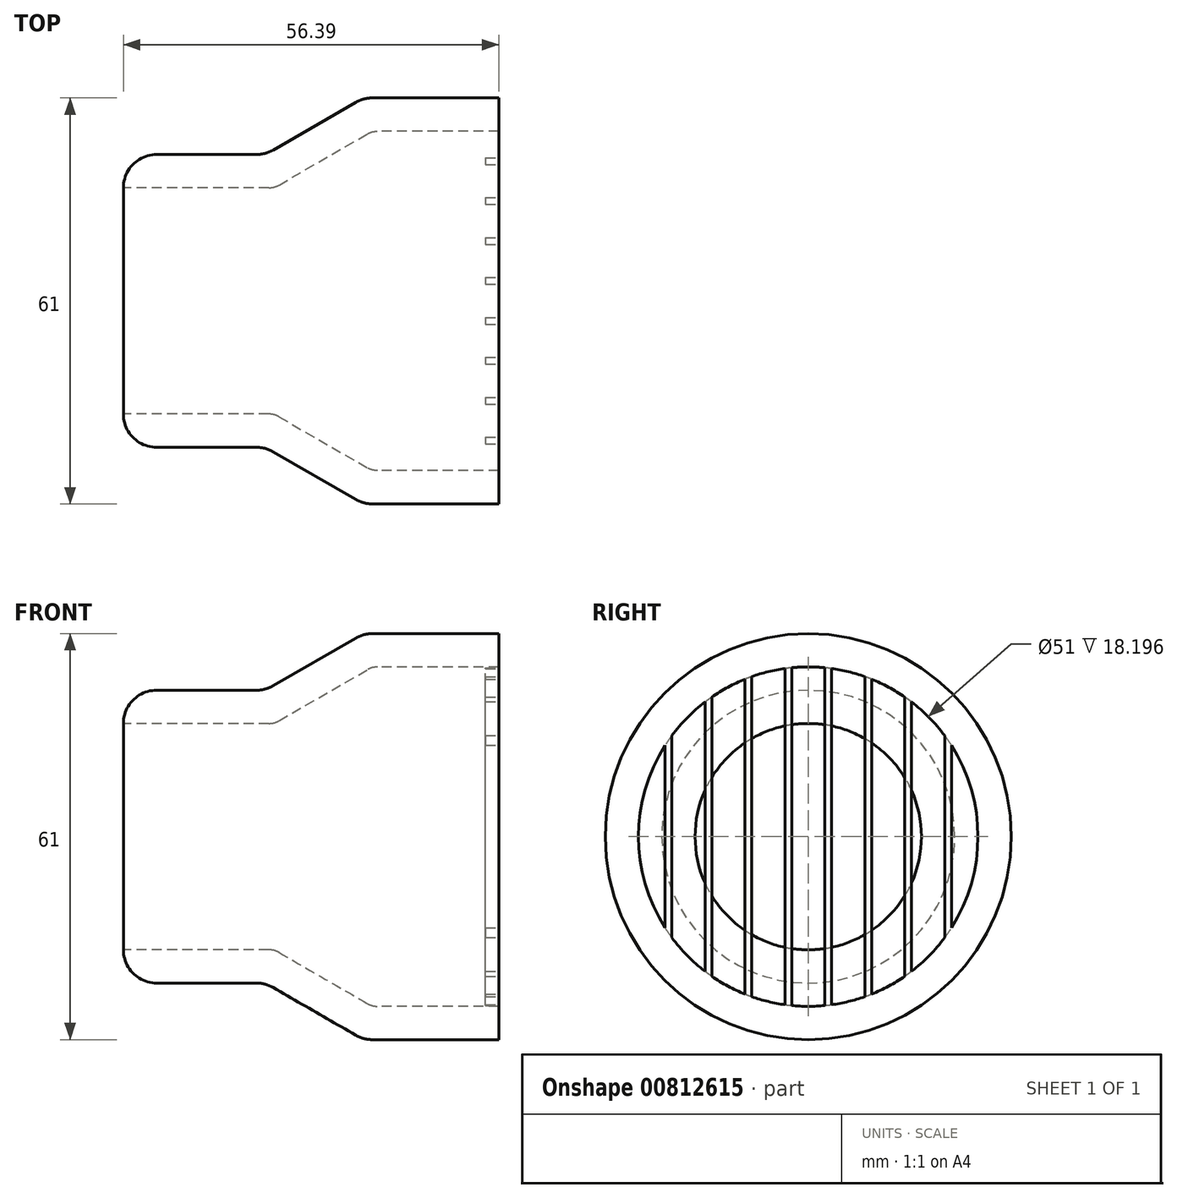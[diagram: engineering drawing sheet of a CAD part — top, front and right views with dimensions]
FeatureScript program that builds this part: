
annotation { "Feature Type Name" : "Feature", "Feature Type Description" : "" }
export const myFeature = defineFeature(function(context is Context, id is Id, definition is map)
    precondition{}
    {
        {
            var Q0;
            Q0=qCreatedBy(makeId("Top.planeOp"),FACE);
            var sketch = newSketch(context, id + "F0", { "sketchPlane" : qUnion([Q0])});
            skLineSegment(sketch, "E0", {"start": v(-22.67, 17) * mm, "end": v(0, 17) * mm});
            skLineSegment(sketch, "E1", {"start": v(0, 17) * mm, "end": v(14.72, 25.5) * mm});
            skLineSegment(sketch, "E2", {"start": v(14.72, 25.5) * mm, "end": v(31.72, 25.5) * mm});
            skLineSegment(sketch, "E3.0", {"start": v(13.38, 30.5) * mm, "end": v(31.72, 30.5) * mm});
            skLineSegment(sketch, "E3.1", {"start": v(-1.34, 22) * mm, "end": v(13.38, 30.5) * mm});
            skLineSegment(sketch, "E3.2", {"start": v(-22.67, 22) * mm, "end": v(-1.34, 22) * mm});
            skLineSegment(sketch, "E4", {"start": v(-22.67, 17) * mm, "end": v(-22.67, 22) * mm});
            skLineSegment(sketch, "E5", {"start": v(31.72, 30.5) * mm, "end": v(31.72, 25.5) * mm});
            skLineSegment(sketch, "E6", {"start": v(-63.57, 0) * mm, "end": v(46.05, 0) * mm});
            skSolve(sketch);
        }
        {
            var Q0;
            Q0=qSketchRegion(id+"F0",true);
            var Q1;
            Q1=sQuery(id+"F0.wireOp",EDGE,"E6");
            revolve(context, id + "F1", {"surfaceOperationType" : NewSurfaceOperationType.NEW, "entities" : qUnion([Q0]), "axis" : qUnion([Q1]), "revolveType" : RevolveType.FULL});
        }
        {
            var Q0;
            Q0=makeQuery(id+"F1.opRevolve","SWEPT_FACE",FACE,{"disambiguationData":[OSD([sQuery(id+"F0.wireOp",EDGE,"E5")])]});
            var sketch = newSketch(context, id + "F2", { "sketchPlane" : qUnion([Q0])});
            skCircle(sketch, "E7.0", {"center": v(0, 0) * mm, "radius": 30.5 * mm});
            skSolve(sketch);
        }
        {
            var Q0;
            Q0=qSketchRegion(id+"F2",true);
            extrude(context, id + "F3", {"entities" : qUnion([Q0]), "operationType" : NewBodyOperationType.ADD, "depth" : 2 * mm, "offsetDistance" : 25 * mm});
        }
        {
            var Q0;
            Q0=makeQuery(id+"F3.opExtrude","CAP_FACE",FACE,{"disambiguationData":[OSD([sQuery(id+"F2.wireOp",EDGE,"E7.0")])],"isStart":false});
            var sketch = newSketch(context, id + "F4", { "sketchPlane" : qUnion([Q0])});
            skLineSegment(sketch, "E8.bottom", {"start": v(-2.5, 25.5) * mm, "end": v(2.5, 25.5) * mm});
            skLineSegment(sketch, "E8.top", {"start": v(-2.5, -25.5) * mm, "end": v(2.5, -25.5) * mm});
            skLineSegment(sketch, "E8.left", {"start": v(-2.5, 25.5) * mm, "end": v(-2.5, -25.5) * mm});
            skLineSegment(sketch, "E8.right", {"start": v(2.5, 25.5) * mm, "end": v(2.5, -25.5) * mm});
            skLineSegment(sketch, "E9.1.0.0", {"start": v(3.5, -25.5) * mm, "end": v(8.5, -25.5) * mm});
            skLineSegment(sketch, "E9.1.0.1", {"start": v(8.5, 25.5) * mm, "end": v(8.5, -25.5) * mm});
            skLineSegment(sketch, "E9.1.0.2", {"start": v(3.5, 25.5) * mm, "end": v(3.5, -25.5) * mm});
            skLineSegment(sketch, "E9.1.0.3", {"start": v(3.5, 25.5) * mm, "end": v(8.5, 25.5) * mm});
            skLineSegment(sketch, "E9.2.0.0", {"start": v(9.5, -25.5) * mm, "end": v(14.5, -25.5) * mm});
            skLineSegment(sketch, "E9.2.0.1", {"start": v(14.5, 25.5) * mm, "end": v(14.5, -25.5) * mm});
            skLineSegment(sketch, "E9.2.0.2", {"start": v(9.5, 25.5) * mm, "end": v(9.5, -25.5) * mm});
            skLineSegment(sketch, "E9.2.0.3", {"start": v(9.5, 25.5) * mm, "end": v(14.5, 25.5) * mm});
            skLineSegment(sketch, "E9.3.0.0", {"start": v(15.5, -25.5) * mm, "end": v(20.5, -25.5) * mm});
            skLineSegment(sketch, "E9.3.0.1", {"start": v(20.5, 25.5) * mm, "end": v(20.5, -25.5) * mm});
            skLineSegment(sketch, "E9.3.0.2", {"start": v(15.5, 25.5) * mm, "end": v(15.5, -25.5) * mm});
            skLineSegment(sketch, "E9.3.0.3", {"start": v(15.5, 25.5) * mm, "end": v(20.5, 25.5) * mm});
            skLineSegment(sketch, "E9.4.0.0", {"start": v(21.5, -25.5) * mm, "end": v(26.5, -25.5) * mm});
            skLineSegment(sketch, "E9.4.0.1", {"start": v(26.5, 25.5) * mm, "end": v(26.5, -25.5) * mm});
            skLineSegment(sketch, "E9.4.0.2", {"start": v(21.5, 25.5) * mm, "end": v(21.5, -25.5) * mm});
            skLineSegment(sketch, "E9.4.0.3", {"start": v(21.5, 25.5) * mm, "end": v(26.5, 25.5) * mm});
            skLineSegment(sketch, "E9.5.0.0", {"start": v(27.5, -25.5) * mm, "end": v(32.5, -25.5) * mm});
            skLineSegment(sketch, "E9.5.0.1", {"start": v(32.5, 25.5) * mm, "end": v(32.5, -25.5) * mm});
            skLineSegment(sketch, "E9.5.0.2", {"start": v(27.5, 25.5) * mm, "end": v(27.5, -25.5) * mm});
            skLineSegment(sketch, "E9.5.0.3", {"start": v(27.5, 25.5) * mm, "end": v(32.5, 25.5) * mm});
            skLineSegment(sketch, "E9.direction1", {"start": v(-2.5, -25.5) * mm, "end": v(3.5, -25.5) * mm, "construction": true});
            skLineSegment(sketch, "E10.1.0.0", {"start": v(-3.5, 25.5) * mm, "end": v(-3.5, -25.5) * mm});
            skLineSegment(sketch, "E10.1.0.1", {"start": v(-8.5, -25.5) * mm, "end": v(-3.5, -25.5) * mm});
            skLineSegment(sketch, "E10.1.0.2", {"start": v(-8.5, 25.5) * mm, "end": v(-8.5, -25.5) * mm});
            skLineSegment(sketch, "E10.1.0.3", {"start": v(-8.5, 25.5) * mm, "end": v(-3.5, 25.5) * mm});
            skLineSegment(sketch, "E10.2.0.0", {"start": v(-9.5, 25.5) * mm, "end": v(-9.5, -25.5) * mm});
            skLineSegment(sketch, "E10.2.0.1", {"start": v(-14.5, -25.5) * mm, "end": v(-9.5, -25.5) * mm});
            skLineSegment(sketch, "E10.2.0.2", {"start": v(-14.5, 25.5) * mm, "end": v(-14.5, -25.5) * mm});
            skLineSegment(sketch, "E10.2.0.3", {"start": v(-14.5, 25.5) * mm, "end": v(-9.5, 25.5) * mm});
            skLineSegment(sketch, "E10.3.0.0", {"start": v(-15.5, 25.5) * mm, "end": v(-15.5, -25.5) * mm});
            skLineSegment(sketch, "E10.3.0.1", {"start": v(-20.5, -25.5) * mm, "end": v(-15.5, -25.5) * mm});
            skLineSegment(sketch, "E10.3.0.2", {"start": v(-20.5, 25.5) * mm, "end": v(-20.5, -25.5) * mm});
            skLineSegment(sketch, "E10.3.0.3", {"start": v(-20.5, 25.5) * mm, "end": v(-15.5, 25.5) * mm});
            skLineSegment(sketch, "E10.4.0.0", {"start": v(-21.5, 25.5) * mm, "end": v(-21.5, -25.5) * mm});
            skLineSegment(sketch, "E10.4.0.1", {"start": v(-26.5, -25.5) * mm, "end": v(-21.5, -25.5) * mm});
            skLineSegment(sketch, "E10.4.0.2", {"start": v(-26.5, 25.5) * mm, "end": v(-26.5, -25.5) * mm});
            skLineSegment(sketch, "E10.4.0.3", {"start": v(-26.5, 25.5) * mm, "end": v(-21.5, 25.5) * mm});
            skLineSegment(sketch, "E10.5.0.0", {"start": v(-27.5, 25.5) * mm, "end": v(-27.5, -25.5) * mm});
            skLineSegment(sketch, "E10.5.0.1", {"start": v(-32.5, -25.5) * mm, "end": v(-27.5, -25.5) * mm});
            skLineSegment(sketch, "E10.5.0.2", {"start": v(-32.5, 25.5) * mm, "end": v(-32.5, -25.5) * mm});
            skLineSegment(sketch, "E10.5.0.3", {"start": v(-32.5, 25.5) * mm, "end": v(-27.5, 25.5) * mm});
            skLineSegment(sketch, "E10.direction1", {"start": v(-2.5, -25.5) * mm, "end": v(-8.5, -25.5) * mm, "construction": true});
            skCircle(sketch, "E11.0", {"center": v(0, 0) * mm, "radius": 30.5 * mm});
            skCircle(sketch, "E12", {"center": v(0, 0) * mm, "radius": 25.5 * mm});
            skSolve(sketch);
        }
        {
            var Q0;
            {var subQ0=sQuery(id+"F4.wireOp",EDGE,"E12");var subQ1=sQuery(id+"F4.wireOp",EDGE,"E9.5.0.2");var subQ2=makeQuery(id+"F4.imprint","INTERSECT",VERTEX,{"disambiguationData":[OD(0.0)],"derivedFrom":[subQ1,subQ0]});Q0=makeQuery(id+"F4.imprint","IMPRINT",FACE,{"disambiguationData":[TD([[makeQuery(id+"F4.imprint","IMPRINT",EDGE,{"disambiguationData":[TD([[subQ2,-1.0]])],"derivedFrom":subQ1}),1.0]])]});}
            var Q1;
            {var subQ0=sQuery(id+"F4.wireOp",EDGE,"E12");var subQ1=sQuery(id+"F4.wireOp",EDGE,"E9.4.0.1");var subQ2=makeQuery(id+"F4.imprint","INTERSECT",VERTEX,{"disambiguationData":[OD(0.0)],"derivedFrom":[subQ1,subQ0]});Q1=makeQuery(id+"F4.imprint","IMPRINT",FACE,{"disambiguationData":[TD([[makeQuery(id+"F4.imprint","IMPRINT",EDGE,{"disambiguationData":[TD([[subQ2,-1.0]])],"derivedFrom":subQ1}),-1.0]])]});}
            var Q2;
            {var subQ0=sQuery(id+"F4.wireOp",EDGE,"E12");var subQ1=sQuery(id+"F4.wireOp",EDGE,"E9.3.0.1");var subQ2=makeQuery(id+"F4.imprint","INTERSECT",VERTEX,{"disambiguationData":[OD(0.0)],"derivedFrom":[subQ1,subQ0]});Q2=makeQuery(id+"F4.imprint","IMPRINT",FACE,{"disambiguationData":[TD([[makeQuery(id+"F4.imprint","IMPRINT",EDGE,{"disambiguationData":[TD([[subQ2,-1.0]])],"derivedFrom":subQ1}),-1.0]])]});}
            var Q3;
            {var subQ0=sQuery(id+"F4.wireOp",EDGE,"E12");var subQ1=sQuery(id+"F4.wireOp",EDGE,"E9.2.0.1");var subQ2=makeQuery(id+"F4.imprint","INTERSECT",VERTEX,{"disambiguationData":[OD(0.0)],"derivedFrom":[subQ1,subQ0]});Q3=makeQuery(id+"F4.imprint","IMPRINT",FACE,{"disambiguationData":[TD([[makeQuery(id+"F4.imprint","IMPRINT",EDGE,{"disambiguationData":[TD([[subQ2,-1.0]])],"derivedFrom":subQ1}),-1.0]])]});}
            var Q4;
            {var subQ0=sQuery(id+"F4.wireOp",EDGE,"E12");var subQ1=sQuery(id+"F4.wireOp",EDGE,"E9.1.0.1");var subQ2=makeQuery(id+"F4.imprint","INTERSECT",VERTEX,{"disambiguationData":[OD(0.0)],"derivedFrom":[subQ1,subQ0]});Q4=makeQuery(id+"F4.imprint","IMPRINT",FACE,{"disambiguationData":[TD([[makeQuery(id+"F4.imprint","IMPRINT",EDGE,{"disambiguationData":[TD([[subQ2,-1.0]])],"derivedFrom":subQ1}),-1.0]])]});}
            var Q5;
            {var subQ0=sQuery(id+"F4.wireOp",EDGE,"E12");var subQ1=sQuery(id+"F4.wireOp",EDGE,"E8.left");var subQ2=makeQuery(id+"F4.imprint","INTERSECT",VERTEX,{"disambiguationData":[OD(0.0)],"derivedFrom":[subQ1,subQ0]});Q5=makeQuery(id+"F4.imprint","IMPRINT",FACE,{"disambiguationData":[TD([[makeQuery(id+"F4.imprint","IMPRINT",EDGE,{"disambiguationData":[TD([[subQ2,-1.0]])],"derivedFrom":subQ1}),1.0]])]});}
            var Q6;
            {var subQ0=sQuery(id+"F4.wireOp",EDGE,"E12");var subQ1=sQuery(id+"F4.wireOp",EDGE,"E10.1.0.0");var subQ2=makeQuery(id+"F4.imprint","INTERSECT",VERTEX,{"disambiguationData":[OD(0.0)],"derivedFrom":[subQ1,subQ0]});Q6=makeQuery(id+"F4.imprint","IMPRINT",FACE,{"disambiguationData":[TD([[makeQuery(id+"F4.imprint","IMPRINT",EDGE,{"disambiguationData":[TD([[subQ2,-1.0]])],"derivedFrom":subQ1}),-1.0]])]});}
            var Q7;
            {var subQ0=sQuery(id+"F4.wireOp",EDGE,"E12");var subQ1=sQuery(id+"F4.wireOp",EDGE,"E10.2.0.0");var subQ2=makeQuery(id+"F4.imprint","INTERSECT",VERTEX,{"disambiguationData":[OD(0.0)],"derivedFrom":[subQ1,subQ0]});Q7=makeQuery(id+"F4.imprint","IMPRINT",FACE,{"disambiguationData":[TD([[makeQuery(id+"F4.imprint","IMPRINT",EDGE,{"disambiguationData":[TD([[subQ2,-1.0]])],"derivedFrom":subQ1}),-1.0]])]});}
            var Q8;
            {var subQ0=sQuery(id+"F4.wireOp",EDGE,"E12");var subQ1=sQuery(id+"F4.wireOp",EDGE,"E10.3.0.0");var subQ2=makeQuery(id+"F4.imprint","INTERSECT",VERTEX,{"disambiguationData":[OD(0.0)],"derivedFrom":[subQ1,subQ0]});Q8=makeQuery(id+"F4.imprint","IMPRINT",FACE,{"disambiguationData":[TD([[makeQuery(id+"F4.imprint","IMPRINT",EDGE,{"disambiguationData":[TD([[subQ2,-1.0]])],"derivedFrom":subQ1}),-1.0]])]});}
            var Q9;
            {var subQ0=sQuery(id+"F4.wireOp",EDGE,"E12");var subQ1=sQuery(id+"F4.wireOp",EDGE,"E10.4.0.0");var subQ2=makeQuery(id+"F4.imprint","INTERSECT",VERTEX,{"disambiguationData":[OD(0.0)],"derivedFrom":[subQ1,subQ0]});Q9=makeQuery(id+"F4.imprint","IMPRINT",FACE,{"disambiguationData":[TD([[makeQuery(id+"F4.imprint","IMPRINT",EDGE,{"disambiguationData":[TD([[subQ2,-1.0]])],"derivedFrom":subQ1}),-1.0]])]});}
            var Q10;
            {var subQ0=sQuery(id+"F4.wireOp",EDGE,"E12");var subQ1=sQuery(id+"F4.wireOp",EDGE,"E10.5.0.0");var subQ2=makeQuery(id+"F4.imprint","INTERSECT",VERTEX,{"disambiguationData":[OD(0.0)],"derivedFrom":[subQ1,subQ0]});Q10=makeQuery(id+"F4.imprint","IMPRINT",FACE,{"disambiguationData":[TD([[makeQuery(id+"F4.imprint","IMPRINT",EDGE,{"disambiguationData":[TD([[subQ2,-1.0]])],"derivedFrom":subQ1}),-1.0]])]});}
            var Q11;
            {var subQ0=sQuery(id+"F4.wireOp",EDGE,"E12");var subQ1=sQuery(id+"F4.wireOp",EDGE,"E9.4.0.2");var subQ2=makeQuery(id+"F4.imprint","INTERSECT",VERTEX,{"disambiguationData":[OD(0.0)],"derivedFrom":[subQ1,subQ0]});Q11=makeQuery(id+"F4.imprint","IMPRINT",FACE,{"disambiguationData":[TD([[makeQuery(id+"F4.imprint","IMPRINT",EDGE,{"disambiguationData":[TD([[subQ2,-1.0]])],"derivedFrom":subQ1}),1.0]])]});}
            var Q12;
            Q12=makeQuery(id+"F3.opExtrude","CAP_FACE",FACE,{"disambiguationData":[OSD([sQuery(id+"F2.wireOp",EDGE,"E7.0")])],"isStart":true});
            extrude(context, id + "F5", {"entities" : qUnion([Q0, Q1, Q2, Q3, Q4, Q5, Q6, Q7, Q8, Q9, Q10, Q11]), "operationType" : NewBodyOperationType.REMOVE, "endBound" : BoundingType.UP_TO_SURFACE, "oppositeDirection" : true, "depth" : 25 * mm, "endBoundEntityFace" : qUnion([Q12]), "offsetDistance" : 25 * mm});
        }
        {
            var Q0;
            Q0=makeQuery(id+"F1.opRevolve","SWEPT_EDGE",EDGE,{"disambiguationData":[OSD([sQuery(id+"F0.wireOp",EDGE,"E3.2"),sQuery(id+"F0.wireOp",EDGE,"E4")])]});
            var Q1;
            Q1=makeQuery(id+"F1.opRevolve","SWEPT_EDGE",EDGE,{"disambiguationData":[OSD([sQuery(id+"F0.wireOp",EDGE,"E3.1"),sQuery(id+"F0.wireOp",EDGE,"E3.2")])]});
            var Q2;
            Q2=makeQuery(id+"F1.opRevolve","SWEPT_EDGE",EDGE,{"disambiguationData":[OSD([sQuery(id+"F0.wireOp",EDGE,"E3.0"),sQuery(id+"F0.wireOp",EDGE,"E3.1")])]});
            fillet(context, id + "F6", {"entities" : qUnion([Q0, Q1, Q2]), "radius" : 5 * mm, "tangentPropagation" : true, "allowEdgeOverflow" : false});
        }
        {
            var Q0;
            Q0=makeQuery(id+"F1.opRevolve","SWEPT_EDGE",EDGE,{"disambiguationData":[OSD([sQuery(id+"F0.wireOp",EDGE,"E1"),sQuery(id+"F0.wireOp",EDGE,"E2")])]});
            var Q1;
            Q1=makeQuery(id+"F1.opRevolve","SWEPT_EDGE",EDGE,{"disambiguationData":[OSD([sQuery(id+"F0.wireOp",EDGE,"E0"),sQuery(id+"F0.wireOp",EDGE,"E1")])]});
            fillet(context, id + "F7", {"entities" : qUnion([Q0, Q1]), "radius" : 3 * mm, "tangentPropagation" : true, "allowEdgeOverflow" : false});
        }
    });
